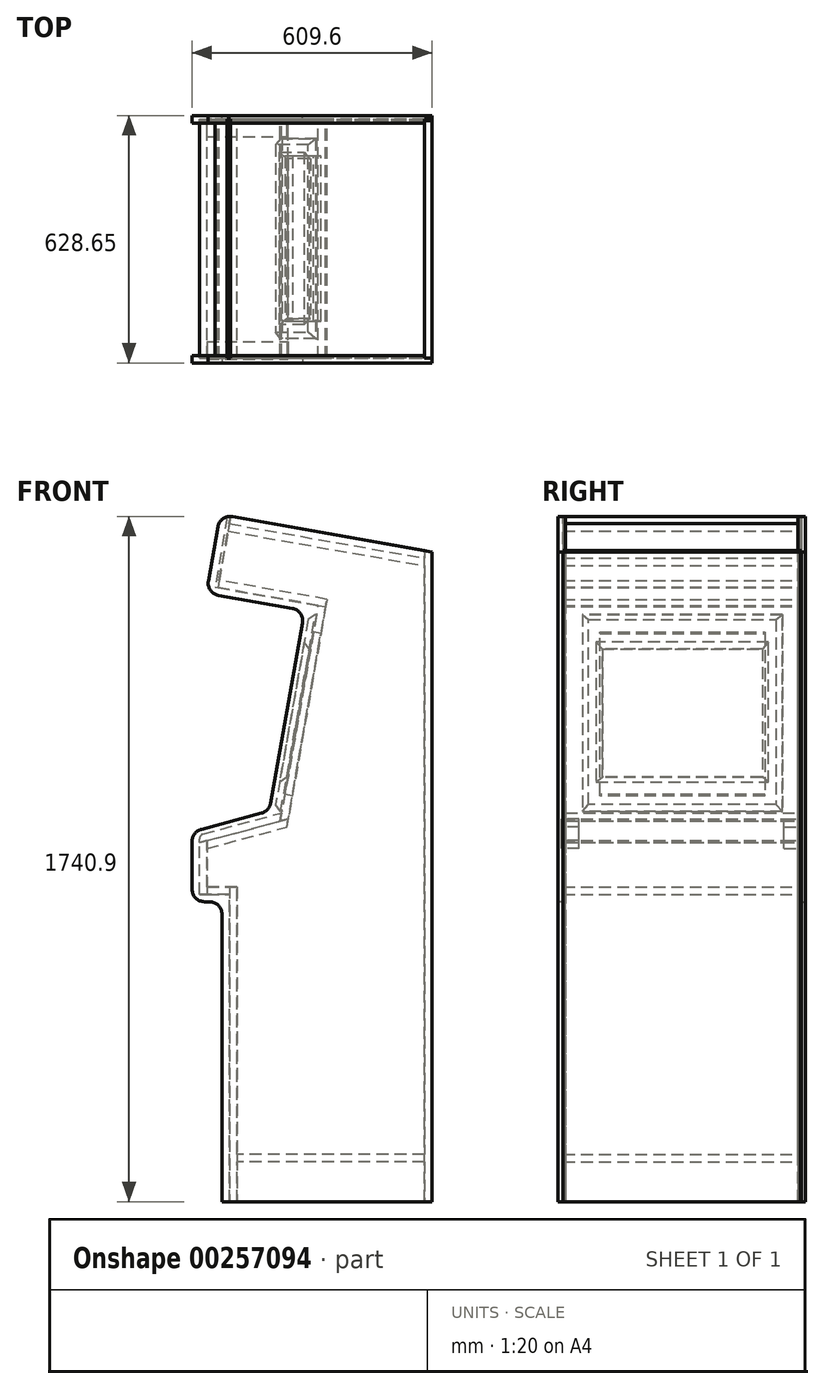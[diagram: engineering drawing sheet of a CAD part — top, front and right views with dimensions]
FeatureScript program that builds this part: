
annotation { "Feature Type Name" : "Feature", "Feature Type Description" : "" }
export const myFeature = defineFeature(function(context is Context, id is Id, definition is map)
    precondition{}
    {
        {
            var Q0;
            Q0=qCreatedBy(makeId("Front.planeOp"),FACE);
            var sketch = newSketch(context, id + "F0", { "sketchPlane" : qUnion([Q0])});
            skLineSegment(sketch, "E0", {"start": v(533.4, 0) * mm, "end": v(533.4, 1651) * mm});
            skLineSegment(sketch, "E1", {"start": v(533.4, 1651) * mm, "end": v(26.3, 1740.42) * mm});
            skLineSegment(sketch, "E2", {"start": v(-10.49, 1714.66) * mm, "end": v(-34.75, 1577.08) * mm});
            skLineSegment(sketch, "E3", {"start": v(-9, 1540.3) * mm, "end": v(178.62, 1507.22) * mm});
            skLineSegment(sketch, "E4", {"start": v(204.37, 1470.44) * mm, "end": v(123.59, 1012.31) * mm});
            skLineSegment(sketch, "E5", {"start": v(100.54, 987.16) * mm, "end": v(-52.67, 946.1) * mm});
            skLineSegment(sketch, "E6", {"start": v(-76.2, 915.44) * mm, "end": v(-76.2, 793.75) * mm});
            skLineSegment(sketch, "E7", {"start": v(-44.45, 762) * mm, "end": v(-31.75, 762) * mm});
            skLineSegment(sketch, "E8", {"start": v(0, 730.25) * mm, "end": v(0, 0) * mm});
            skLineSegment(sketch, "E9", {"start": v(0, 0) * mm, "end": v(533.4, 0) * mm});
            skPoint(sketch, "E10.visualSharp", {"position": v(-4.97, 1745.93) * mm});
            skArc(sketch, "E10.filletArc", {"start": v(26.3, 1740.42) * mm, "mid": v(2.57, 1735.16) * mm, "end": v(-10.49, 1714.66) * mm});
            skPoint(sketch, "E11.visualSharp", {"position": v(-40.26, 1545.82) * mm});
            skArc(sketch, "E11.filletArc", {"start": v(-34.75, 1577.08) * mm, "mid": v(-29.49, 1553.36) * mm, "end": v(-9, 1540.3) * mm});
            skPoint(sketch, "E12.visualSharp", {"position": v(209.88, 1501.71) * mm});
            skArc(sketch, "E12.filletArc", {"start": v(204.37, 1470.44) * mm, "mid": v(199.1, 1494.17) * mm, "end": v(178.62, 1507.22) * mm});
            skPoint(sketch, "E13.visualSharp", {"position": v(120.08, 992.4) * mm});
            skArc(sketch, "E13.filletArc", {"start": v(100.54, 987.16) * mm, "mid": v(115.73, 996.38) * mm, "end": v(123.59, 1012.31) * mm});
            skPoint(sketch, "E14.visualSharp", {"position": v(-76.2, 939.8) * mm});
            skArc(sketch, "E14.filletArc", {"start": v(-52.67, 946.1) * mm, "mid": v(-69.64, 934.77) * mm, "end": v(-76.2, 915.44) * mm});
            skPoint(sketch, "E15.visualSharp", {"position": v(-76.2, 762) * mm});
            skArc(sketch, "E15.filletArc", {"start": v(-76.2, 793.75) * mm, "mid": v(-66.9, 771.3) * mm, "end": v(-44.45, 762) * mm});
            skPoint(sketch, "E16.visualSharp", {"position": v(0, 762) * mm});
            skArc(sketch, "E16.filletArc", {"start": v(0, 730.25) * mm, "mid": v(-9.3, 752.7) * mm, "end": v(-31.75, 762) * mm});
            skSolve(sketch);
        }
        {
            var Q0;
            Q0=makeQuery(id+"F0.imprint","IMPRINT",FACE,{"disambiguationData":[TD([[makeQuery(id+"F0.imprint","IMPRINT",EDGE,{"derivedFrom":sQuery(id+"F0.wireOp",EDGE,"E0")}),1.0]])]});
            extrude(context, id + "F1", {"entities" : qUnion([Q0]), "depth" : 19.05 * mm});
        }
        {
            var Q0;
            Q0=makeQuery(id+"F1.opExtrude","CAP_FACE",FACE,{"disambiguationData":[OSD([sQuery(id+"F0.wireOp",EDGE,"E0"),sQuery(id+"F0.wireOp",EDGE,"E1"),sQuery(id+"F0.wireOp",EDGE,"E2"),sQuery(id+"F0.wireOp",EDGE,"E3"),sQuery(id+"F0.wireOp",EDGE,"E4"),sQuery(id+"F0.wireOp",EDGE,"E5"),sQuery(id+"F0.wireOp",EDGE,"E6"),sQuery(id+"F0.wireOp",EDGE,"E7"),sQuery(id+"F0.wireOp",EDGE,"E8"),sQuery(id+"F0.wireOp",EDGE,"E9")])],"isStart":false});
            var sketch = newSketch(context, id + "F2", { "sketchPlane" : qUnion([Q0])});
            skLineSegment(sketch, "E17", {"start": v(514.35, 1654.36) * mm, "end": v(514.35, 0) * mm});
            skLineSegment(sketch, "E18", {"start": v(514.35, 101.6) * mm, "end": v(38.1, 101.6) * mm});
            skLineSegment(sketch, "E19", {"start": v(19.05, 0) * mm, "end": v(19.05, 800.1) * mm});
            skLineSegment(sketch, "E20", {"start": v(19.05, 781.05) * mm, "end": v(-57.15, 781.05) * mm});
            skLineSegment(sketch, "E21", {"start": v(-57.15, 781.05) * mm, "end": v(-57.15, 912.03) * mm});
            skLineSegment(sketch, "E22", {"start": v(-57.15, 912.03) * mm, "end": v(168.13, 972.4) * mm});
            skLineSegment(sketch, "E23", {"start": v(147.83, 966.96) * mm, "end": v(244.46, 1514.96) * mm});
            skLineSegment(sketch, "E24", {"start": v(263.22, 1511.65) * mm, "end": v(-18.19, 1561.27) * mm});
            skLineSegment(sketch, "E25", {"start": v(-18.19, 1561.27) * mm, "end": v(10.48, 1723.86) * mm});
            skLineSegment(sketch, "E26", {"start": v(18.28, 1722.49) * mm, "end": v(514.35, 1635.02) * mm});
            skLineSegment(sketch, "E27.0", {"start": v(266.53, 1530.4) * mm, "end": v(-7.08, 1578.65) * mm});
            skLineSegment(sketch, "E27.1", {"start": v(164.48, 951.7) * mm, "end": v(266.53, 1530.4) * mm});
            skLineSegment(sketch, "E27.2", {"start": v(38.1, 0) * mm, "end": v(38.1, 800.1) * mm});
            skLineSegment(sketch, "E27.3", {"start": v(38.1, 800.1) * mm, "end": v(-38.1, 800.1) * mm});
            skLineSegment(sketch, "E27.4", {"start": v(-38.1, 781.05) * mm, "end": v(-38.1, 917.14) * mm});
            skLineSegment(sketch, "E27.5", {"start": v(-38.1, 897.42) * mm, "end": v(164.48, 951.7) * mm});
            skLineSegment(sketch, "E28.0", {"start": v(14.98, 1703.72) * mm, "end": v(514.35, 1615.67) * mm});
            skLineSegment(sketch, "E28.1", {"start": v(-10.39, 1559.9) * mm, "end": v(18.28, 1722.49) * mm});
            skLineSegment(sketch, "E29.0", {"start": v(514.35, 120.65) * mm, "end": v(38.1, 120.65) * mm});
            skLineSegment(sketch, "E30", {"start": v(18.28, 1722.49) * mm, "end": v(21.53, 1740.89) * mm});
            skLineSegment(sketch, "E31", {"start": v(13.33, 1740.01) * mm, "end": v(10.48, 1723.86) * mm});
            skSolve(sketch);
        }
        {
            var Q0;
            {var subQ0=sQuery(id+"F2.wireOp",EDGE,"E17");Q0=makeQuery(id+"F2.imprint","IMPRINT",FACE,{"disambiguationData":[TD([[makeQuery(id+"F2.imprint","IMPRINT",EDGE,{"derivedFrom":subQ0}),1.0]])]});}
            var Q1;
            {var subQ0=sQuery(id+"F2.wireOp",EDGE,"E18");Q1=makeQuery(id+"F2.imprint","IMPRINT",FACE,{"disambiguationData":[TD([[makeQuery(id+"F2.imprint","IMPRINT",EDGE,{"derivedFrom":subQ0}),-1.0]])]});}
            var Q2;
            {var subQ7=sQuery(id+"F2.wireOp",EDGE,"E19");Q2=makeQuery(id+"F2.imprint","IMPRINT",FACE,{"disambiguationData":[TD([[makeQuery(id+"F2.imprint","IMPRINT",EDGE,{"derivedFrom":subQ7}),-1.0]])]});}
            var Q3;
            {var subQ0=sQuery(id+"F2.wireOp",EDGE,"E27.3");var subQ1=sQuery(id+"F2.wireOp",EDGE,"E19");var subQ2=makeQuery(id+"F2.imprint","INTERSECT",VERTEX,{"derivedFrom":[subQ1,subQ0]});Q3=makeQuery(id+"F2.imprint","IMPRINT",FACE,{"disambiguationData":[TD([[makeQuery(id+"F2.imprint","IMPRINT",EDGE,{"disambiguationData":[TD([[subQ2,1.0]])],"derivedFrom":subQ1}),1.0]])]});}
            var Q4;
            {var subQ4=sQuery(id+"F2.wireOp",EDGE,"E21");var subQ5=sQuery(id+"F2.wireOp",EDGE,"E20");var subQ6=makeQuery(id+"F2.imprint","INTERSECT",VERTEX,{"derivedFrom":[subQ5,subQ4]});Q4=makeQuery(id+"F2.imprint","IMPRINT",FACE,{"disambiguationData":[TD([[makeQuery(id+"F2.imprint","IMPRINT",EDGE,{"disambiguationData":[TD([[subQ6,1.0]])],"derivedFrom":subQ5}),-1.0]])]});}
            var Q5;
            {var subQ1=sQuery(id+"F2.wireOp",EDGE,"E22");var subQ6=sQuery(id+"F2.wireOp",EDGE,"E21");var subQ9=makeQuery(id+"F2.imprint","INTERSECT",VERTEX,{"derivedFrom":[subQ6,subQ1]});Q5=makeQuery(id+"F2.imprint","IMPRINT",FACE,{"disambiguationData":[TD([[makeQuery(id+"F2.imprint","IMPRINT",EDGE,{"disambiguationData":[TD([[subQ9,1.0]])],"derivedFrom":subQ6}),-1.0]])]});}
            var Q6;
            {var subQ3=sQuery(id+"F2.wireOp",EDGE,"E23");Q6=makeQuery(id+"F2.imprint","IMPRINT",FACE,{"disambiguationData":[TD([[makeQuery(id+"F2.imprint","IMPRINT",EDGE,{"derivedFrom":subQ3}),-1.0]])]});}
            var Q7;
            {var subQ0=sQuery(id+"F2.wireOp",EDGE,"E27.0");Q7=makeQuery(id+"F2.imprint","IMPRINT",FACE,{"disambiguationData":[TD([[makeQuery(id+"F2.imprint","IMPRINT",EDGE,{"derivedFrom":subQ0}),1.0]])]});}
            var Q8;
            {var subQ5=sQuery(id+"F2.wireOp",EDGE,"E25");Q8=makeQuery(id+"F2.imprint","IMPRINT",FACE,{"disambiguationData":[TD([[makeQuery(id+"F2.imprint","IMPRINT",EDGE,{"derivedFrom":subQ5}),-1.0]])]});}
            var Q9;
            {var subQ3=sQuery(id+"F2.wireOp",EDGE,"E28.0");Q9=makeQuery(id+"F2.imprint","IMPRINT",FACE,{"disambiguationData":[TD([[makeQuery(id+"F2.imprint","IMPRINT",EDGE,{"derivedFrom":subQ3}),1.0]])]});}
            var Q10;
            {var subQ2=sQuery(id+"F2.wireOp",EDGE,"E30");Q10=makeQuery(id+"F2.imprint","IMPRINT",FACE,{"disambiguationData":[TD([[makeQuery(id+"F2.imprint","IMPRINT",EDGE,{"derivedFrom":subQ2}),1.0]])]});}
            var Q11;
            {var subQ3=sQuery(id+"F2.wireOp",EDGE,"E27.5");Q11=makeQuery(id+"F2.imprint","IMPRINT",FACE,{"disambiguationData":[TD([[makeQuery(id+"F2.imprint","IMPRINT",EDGE,{"derivedFrom":subQ3}),1.0]])]});}
            extrude(context, id + "F3", {"entities" : qUnion([Q0, Q1, Q2, Q3, Q4, Q5, Q6, Q7, Q8, Q9, Q10, Q11]), "operationType" : NewBodyOperationType.REMOVE, "oppositeDirection" : true, "depth" : 6.35 * mm});
        }
        {
            var Q0;
            Q0=makeQuery(id+"F3.boolean.opBoolean","SPLIT",FACE,{"disambiguationData":[TD([makeQuery(id+"F3.opExtrude","SWEPT_FACE",FACE,{"disambiguationData":[OSD([sQuery(id+"F2.wireOp",EDGE,"E27.0")])]})])],"derivedFrom":makeQuery(id+"F1.opExtrude","CAP_FACE",FACE,{"disambiguationData":[OSD([sQuery(id+"F0.wireOp",EDGE,"E0"),sQuery(id+"F0.wireOp",EDGE,"E1"),sQuery(id+"F0.wireOp",EDGE,"E2"),sQuery(id+"F0.wireOp",EDGE,"E3"),sQuery(id+"F0.wireOp",EDGE,"E4"),sQuery(id+"F0.wireOp",EDGE,"E5"),sQuery(id+"F0.wireOp",EDGE,"E6"),sQuery(id+"F0.wireOp",EDGE,"E7"),sQuery(id+"F0.wireOp",EDGE,"E8"),sQuery(id+"F0.wireOp",EDGE,"E9"),sQuery(id+"F0.wireOp",EDGE,"E10.filletArc"),sQuery(id+"F0.wireOp",EDGE,"E11.filletArc"),sQuery(id+"F0.wireOp",EDGE,"E12.filletArc"),sQuery(id+"F0.wireOp",EDGE,"E13.filletArc"),sQuery(id+"F0.wireOp",EDGE,"E14.filletArc"),sQuery(id+"F0.wireOp",EDGE,"E15.filletArc"),sQuery(id+"F0.wireOp",EDGE,"E16.filletArc")])],"isStart":false})});
            cPlane(context, id + "F4", {"entities" : qUnion([Q0]), "cplaneType" : CPlaneType.OFFSET, "offset" : 295.27 * mm, "width" : 152.4 * mm, "height" : 152.4 * mm});
        }
        {
            var Q0;
            Q0=makeQuery(id+"F1.opExtrude","SWEPT_BODY",BODY,{"disambiguationData":[OSD([sQuery(id+"F0.wireOp",EDGE,"E0"),sQuery(id+"F0.wireOp",EDGE,"E1"),sQuery(id+"F0.wireOp",EDGE,"E2"),sQuery(id+"F0.wireOp",EDGE,"E3"),sQuery(id+"F0.wireOp",EDGE,"E4"),sQuery(id+"F0.wireOp",EDGE,"E5"),sQuery(id+"F0.wireOp",EDGE,"E6"),sQuery(id+"F0.wireOp",EDGE,"E7"),sQuery(id+"F0.wireOp",EDGE,"E8"),sQuery(id+"F0.wireOp",EDGE,"E9")])]});
            var Q1;
            Q1=qCreatedBy(id+"F4.planeOp",FACE);
            mirror(context, id + "F5", {"entities" : qUnion([Q0]), "mirrorPlane" : qUnion([Q1])});
        }
        {
            var Q0;
            {var subQ3=sQuery(id+"F2.wireOp",EDGE,"E28.0");Q0=makeQuery(id+"F2.imprint","IMPRINT",FACE,{"disambiguationData":[TD([[makeQuery(id+"F2.imprint","IMPRINT",EDGE,{"derivedFrom":subQ3}),1.0]])]});}
            extrude(context, id + "F6", {"entities" : qUnion([Q0]), "endBound" : BoundingType.UP_TO_NEXT, "depth" : 25.4 * mm, "hasSecondDirection" : true, "secondDirectionOppositeDirection" : true, "secondDirectionDepth" : 9.52 * mm});
        }
        {
            var Q0;
            {var subQ5=sQuery(id+"F2.wireOp",EDGE,"E25");Q0=makeQuery(id+"F2.imprint","IMPRINT",FACE,{"disambiguationData":[TD([[makeQuery(id+"F2.imprint","IMPRINT",EDGE,{"derivedFrom":subQ5}),-1.0]])]});}
            extrude(context, id + "F7", {"entities" : qUnion([Q0]), "endBound" : BoundingType.UP_TO_NEXT, "depth" : 25.4 * mm, "hasSecondDirection" : true, "secondDirectionOppositeDirection" : true, "secondDirectionDepth" : 9.52 * mm});
        }
        {
            var Q0;
            {var subQ0=sQuery(id+"F2.wireOp",EDGE,"E27.0");Q0=makeQuery(id+"F2.imprint","IMPRINT",FACE,{"disambiguationData":[TD([[makeQuery(id+"F2.imprint","IMPRINT",EDGE,{"derivedFrom":subQ0}),1.0]])]});}
            extrude(context, id + "F8", {"entities" : qUnion([Q0]), "endBound" : BoundingType.UP_TO_NEXT, "depth" : 25.4 * mm, "hasSecondDirection" : true, "secondDirectionOppositeDirection" : true, "secondDirectionDepth" : 9.52 * mm});
        }
        {
            var Q0;
            {var subQ3=sQuery(id+"F2.wireOp",EDGE,"E23");Q0=makeQuery(id+"F2.imprint","IMPRINT",FACE,{"disambiguationData":[TD([[makeQuery(id+"F2.imprint","IMPRINT",EDGE,{"derivedFrom":subQ3}),-1.0]])]});}
            extrude(context, id + "F9", {"entities" : qUnion([Q0]), "endBound" : BoundingType.UP_TO_NEXT, "depth" : 25.4 * mm, "hasSecondDirection" : true, "secondDirectionOppositeDirection" : true, "secondDirectionDepth" : 9.52 * mm});
        }
        {
            var Q0;
            Q0=makeQuery(id+"F9.opExtrude","SWEPT_FACE",FACE,{"disambiguationData":[OSD([sQuery(id+"F2.wireOp",EDGE,"E23")])]});
            var sketch = newSketch(context, id + "F10", { "sketchPlane" : qUnion([Q0])});
            skLineSegment(sketch, "E32", {"start": v(103.19, 1465.72) * mm, "end": v(103.19, 1046.62) * mm});
            skLineSegment(sketch, "E33", {"start": v(103.19, 1046.62) * mm, "end": v(522.29, 1046.62) * mm});
            skLineSegment(sketch, "E34", {"start": v(522.29, 1046.62) * mm, "end": v(522.29, 1465.72) * mm});
            skLineSegment(sketch, "E35", {"start": v(522.29, 1465.72) * mm, "end": v(103.19, 1465.72) * mm});
            skLineSegment(sketch, "E36", {"start": v(312.74, 977.94) * mm, "end": v(312.74, 1046.62) * mm, "construction": true});
            skLineSegment(sketch, "E37", {"start": v(615.95, 1256.17) * mm, "end": v(522.29, 1256.17) * mm, "construction": true});
            skSolve(sketch);
        }
        {
            var Q0;
            Q0=makeQuery(id+"F10.imprint","IMPRINT",FACE,{"disambiguationData":[TD([[makeQuery(id+"F10.imprint","IMPRINT",EDGE,{"derivedFrom":sQuery(id+"F10.wireOp",EDGE,"E32")}),1.0]])]});
            extrude(context, id + "F11", {"entities" : qUnion([Q0]), "operationType" : NewBodyOperationType.REMOVE, "oppositeDirection" : true, "depth" : 25.4 * mm});
        }
        {
            var Q0;
            {var subQ3=sQuery(id+"F2.wireOp",EDGE,"E27.5");Q0=makeQuery(id+"F2.imprint","IMPRINT",FACE,{"disambiguationData":[TD([[makeQuery(id+"F2.imprint","IMPRINT",EDGE,{"derivedFrom":subQ3}),1.0]])]});}
            extrude(context, id + "F12", {"entities" : qUnion([Q0]), "depth" : 34.92 * mm, "hasSecondDirection" : true, "secondDirectionOppositeDirection" : true, "secondDirectionDepth" : 9.52 * mm});
        }
        {
            var Q0;
            {var subQ4=sQuery(id+"F2.wireOp",EDGE,"E21");var subQ5=sQuery(id+"F2.wireOp",EDGE,"E20");var subQ6=makeQuery(id+"F2.imprint","INTERSECT",VERTEX,{"derivedFrom":[subQ5,subQ4]});Q0=makeQuery(id+"F2.imprint","IMPRINT",FACE,{"disambiguationData":[TD([[makeQuery(id+"F2.imprint","IMPRINT",EDGE,{"disambiguationData":[TD([[subQ6,1.0]])],"derivedFrom":subQ5}),-1.0]])]});}
            extrude(context, id + "F13", {"entities" : qUnion([Q0]), "endBound" : BoundingType.UP_TO_NEXT, "depth" : 25.4 * mm, "hasSecondDirection" : true, "secondDirectionOppositeDirection" : true, "secondDirectionDepth" : 9.52 * mm});
        }
        {
            var Q0;
            {var subQ0=sQuery(id+"F2.wireOp",EDGE,"E27.3");var subQ1=sQuery(id+"F2.wireOp",EDGE,"E19");var subQ2=makeQuery(id+"F2.imprint","INTERSECT",VERTEX,{"derivedFrom":[subQ1,subQ0]});Q0=makeQuery(id+"F2.imprint","IMPRINT",FACE,{"disambiguationData":[TD([[makeQuery(id+"F2.imprint","IMPRINT",EDGE,{"disambiguationData":[TD([[subQ2,1.0]])],"derivedFrom":subQ1}),1.0]])]});}
            extrude(context, id + "F14", {"entities" : qUnion([Q0]), "endBound" : BoundingType.UP_TO_NEXT, "depth" : 25.4 * mm, "hasSecondDirection" : true, "secondDirectionOppositeDirection" : true, "secondDirectionDepth" : 9.52 * mm});
        }
        {
            var Q0;
            {var subQ3=makeQuery(id+"F1.opExtrude","CAP_EDGE",EDGE,{"disambiguationData":[OSD([sQuery(id+"F0.wireOp",EDGE,"E9")])],"isStart":false});var subQ6=sQuery(id+"F2.wireOp",EDGE,"E19");var subQ9=makeQuery(id+"F2.imprint","INTERSECT",VERTEX,{"derivedFrom":[subQ3,subQ6]});Q0=makeQuery(id+"F2.imprint","IMPRINT",FACE,{"disambiguationData":[TD([[makeQuery(id+"F2.imprint","IMPRINT",EDGE,{"disambiguationData":[TD([[subQ9,-1.0]])],"derivedFrom":subQ6}),-1.0]])]});}
            extrude(context, id + "F15", {"entities" : qUnion([Q0]), "endBound" : BoundingType.UP_TO_NEXT, "depth" : 25.4 * mm, "hasSecondDirection" : true, "secondDirectionOppositeDirection" : true, "secondDirectionDepth" : 9.52 * mm});
        }
        {
            var Q0;
            {var subQ0=sQuery(id+"F2.wireOp",EDGE,"E18");Q0=makeQuery(id+"F2.imprint","IMPRINT",FACE,{"disambiguationData":[TD([[makeQuery(id+"F2.imprint","IMPRINT",EDGE,{"derivedFrom":subQ0}),-1.0]])]});}
            extrude(context, id + "F16", {"entities" : qUnion([Q0]), "endBound" : BoundingType.UP_TO_NEXT, "depth" : 25.4 * mm, "hasSecondDirection" : true, "secondDirectionOppositeDirection" : true, "secondDirectionDepth" : 9.52 * mm});
        }
        {
            var Q0;
            {var subQ9=makeQuery(id+"F1.opExtrude","CAP_EDGE",EDGE,{"disambiguationData":[OSD([sQuery(id+"F0.wireOp",EDGE,"E0")])],"isStart":false});Q0=makeQuery(id+"F2.imprint","IMPRINT",FACE,{"disambiguationData":[TD([[makeQuery(id+"F2.imprint","IMPRINT",EDGE,{"derivedFrom":subQ9}),1.0]])]});}
            extrude(context, id + "F17", {"entities" : qUnion([Q0]), "endBound" : BoundingType.UP_TO_NEXT, "depth" : 25.4 * mm, "hasSecondDirection" : true, "secondDirectionOppositeDirection" : true, "secondDirectionDepth" : 9.52 * mm});
        }
        {
            var Q0;
            Q0=makeQuery(id+"F12.opExtrude","SWEPT_BODY",BODY,{"disambiguationData":[OSD([sQuery(id+"F2.wireOp",EDGE,"E22"),sQuery(id+"F2.wireOp",EDGE,"E27.1"),sQuery(id+"F2.wireOp",EDGE,"E27.4"),sQuery(id+"F2.wireOp",EDGE,"E27.5")])]});
            var Q1;
            Q1=qCreatedBy(id+"F4.planeOp",FACE);
            mirror(context, id + "F18", {"entities" : qUnion([Q0]), "mirrorPlane" : qUnion([Q1])});
        }
        {
            var Q0;
            {var subQ1=sQuery(id+"F2.wireOp",EDGE,"E21");Q0=makeQuery(id+"F2.imprint","IMPRINT",FACE,{"disambiguationData":[TD([[makeQuery(id+"F2.imprint","IMPRINT",EDGE,{"derivedFrom":subQ1}),1.0]])]});}
            var sketch = newSketch(context, id + "F19", { "sketchPlane" : qUnion([Q0])});
            skLineSegment(sketch, "E38", {"start": v(-57.15, 912.03) * mm, "end": v(147.83, 966.96) * mm});
            skLineSegment(sketch, "E39", {"start": v(147.83, 966.96) * mm, "end": v(151.48, 987.66) * mm});
            skLineSegment(sketch, "E40", {"start": v(151.48, 987.66) * mm, "end": v(-47.74, 934.28) * mm});
            skLineSegment(sketch, "E41", {"start": v(-57.15, 922.01) * mm, "end": v(-57.15, 912.03) * mm});
            skPoint(sketch, "E42.visualSharp", {"position": v(-57.15, 931.76) * mm});
            skArc(sketch, "E42.filletArc", {"start": v(-47.74, 934.28) * mm, "mid": v(-54.53, 929.74) * mm, "end": v(-57.15, 922.01) * mm});
            skSolve(sketch);
        }
        {
            var Q0;
            {var subQ0=sQuery(id+"F19.wireOp",EDGE,"E39");Q0=makeQuery(id+"F19.imprint","IMPRINT",FACE,{"disambiguationData":[TD([[makeQuery(id+"F19.imprint","IMPRINT",EDGE,{"derivedFrom":subQ0}),1.0]])]});}
            extrude(context, id + "F20", {"entities" : qUnion([Q0]), "endBound" : BoundingType.UP_TO_NEXT, "depth" : 25.4 * mm});
        }
        {
            var Q0;
            Q0=makeQuery(id+"F9.opExtrude","SWEPT_FACE",FACE,{"disambiguationData":[OSD([sQuery(id+"F2.wireOp",EDGE,"E23")])]});
            var sketch = newSketch(context, id + "F21", { "sketchPlane" : qUnion([Q0])});
            skLineSegment(sketch, "E43.bottom", {"start": v(58.74, 1510.17) * mm, "end": v(566.74, 1510.17) * mm});
            skLineSegment(sketch, "E43.top", {"start": v(58.74, 1002.17) * mm, "end": v(566.74, 1002.17) * mm});
            skLineSegment(sketch, "E43.left", {"start": v(58.74, 1510.17) * mm, "end": v(58.74, 1002.17) * mm});
            skLineSegment(sketch, "E43.right", {"start": v(566.74, 1510.17) * mm, "end": v(566.74, 1002.17) * mm});
            skLineSegment(sketch, "E44.bottom", {"start": v(109.54, 1421.27) * mm, "end": v(515.94, 1421.27) * mm});
            skLineSegment(sketch, "E44.top", {"start": v(109.54, 1091.07) * mm, "end": v(515.94, 1091.07) * mm});
            skLineSegment(sketch, "E44.left", {"start": v(109.54, 1421.27) * mm, "end": v(109.54, 1091.07) * mm});
            skLineSegment(sketch, "E44.right", {"start": v(515.94, 1421.27) * mm, "end": v(515.94, 1091.07) * mm});
            skLineSegment(sketch, "E45", {"start": v(312.74, 1510.17) * mm, "end": v(312.74, 1421.27) * mm, "construction": true});
            skLineSegment(sketch, "E46", {"start": v(109.54, 1256.17) * mm, "end": v(58.74, 1256.17) * mm, "construction": true});
            skSolve(sketch);
        }
        {
            var Q0;
            Q0=makeQuery(id+"F21.imprint","IMPRINT",FACE,{"disambiguationData":[TD([[makeQuery(id+"F21.imprint","IMPRINT",EDGE,{"derivedFrom":sQuery(id+"F21.wireOp",EDGE,"E44.bottom")}),1.0]])]});
            var Q1;
            Q1=makeQuery(id+"F21.imprint","IMPRINT",FACE,{"disambiguationData":[TD([[makeQuery(id+"F21.imprint","IMPRINT",EDGE,{"derivedFrom":sQuery(id+"F21.wireOp",EDGE,"E43.bottom")}),-1.0]])]});
            var Q2;
            Q2=sQuery(id+"F21.wireOp",EDGE,"E46");
            extrude(context, id + "F22", {"entities" : qUnion([Q0, Q1]), "surfaceEntities" : qUnion([Q2]), "depth" : 19.05 * mm});
        }
        {
            var Q0;
            Q0=makeQuery(id+"F22.opExtrude","CAP_EDGE",EDGE,{"disambiguationData":[OSD([sQuery(id+"F21.wireOp",EDGE,"E44.bottom")])],"isStart":false});
            var Q1;
            Q1=makeQuery(id+"F22.opExtrude","CAP_EDGE",EDGE,{"disambiguationData":[OSD([sQuery(id+"F21.wireOp",EDGE,"E44.left")])],"isStart":false});
            var Q2;
            Q2=makeQuery(id+"F22.opExtrude","CAP_EDGE",EDGE,{"disambiguationData":[OSD([sQuery(id+"F21.wireOp",EDGE,"E44.top")])],"isStart":false});
            var Q3;
            Q3=makeQuery(id+"F22.opExtrude","CAP_EDGE",EDGE,{"disambiguationData":[OSD([sQuery(id+"F21.wireOp",EDGE,"E44.right")])],"isStart":false});
            chamfer(context, id + "F23", {"entities" : qUnion([Q0, Q1, Q2, Q3]), "width" : 15.88 * mm, "tangentPropagation" : true});
        }
        {
            var Q0;
            Q0=makeQuery(id+"F22.opExtrude","CAP_EDGE",EDGE,{"disambiguationData":[OSD([sQuery(id+"F21.wireOp",EDGE,"E43.right")])],"isStart":false});
            var Q1;
            Q1=makeQuery(id+"F22.opExtrude","CAP_EDGE",EDGE,{"disambiguationData":[OSD([sQuery(id+"F21.wireOp",EDGE,"E43.bottom")])],"isStart":false});
            var Q2;
            Q2=makeQuery(id+"F22.opExtrude","CAP_EDGE",EDGE,{"disambiguationData":[OSD([sQuery(id+"F21.wireOp",EDGE,"E43.left")])],"isStart":false});
            var Q3;
            Q3=makeQuery(id+"F22.opExtrude","CAP_EDGE",EDGE,{"disambiguationData":[OSD([sQuery(id+"F21.wireOp",EDGE,"E43.top")])],"isStart":false});
            chamfer(context, id + "F24", {"entities" : qUnion([Q0, Q1, Q2, Q3]), "width" : 15.88 * mm, "tangentPropagation" : true});
        }
    });
